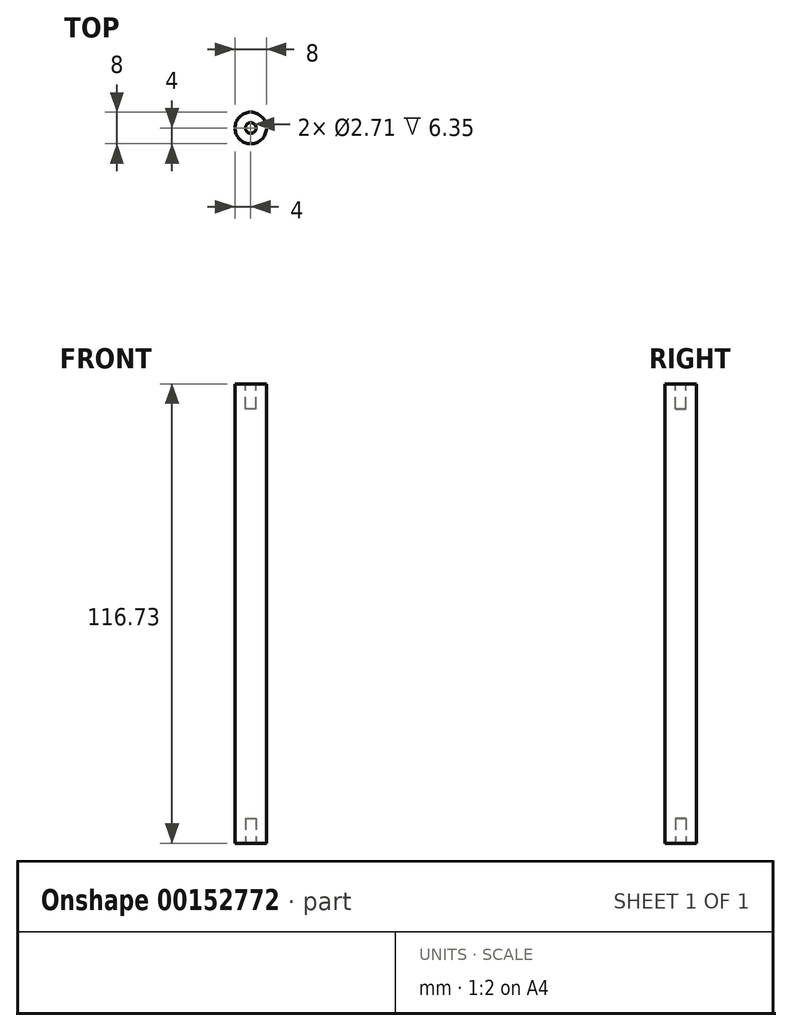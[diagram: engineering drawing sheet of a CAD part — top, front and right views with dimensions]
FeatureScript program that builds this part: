
annotation { "Feature Type Name" : "Feature", "Feature Type Description" : "" }
export const myFeature = defineFeature(function(context is Context, id is Id, definition is map)
    precondition{}
    {
        {
            var Q0;
            Q0=qCreatedBy(makeId("Top.planeOp"),FACE);
            var sketch = newSketch(context, id + "F0", { "sketchPlane" : qUnion([Q0])});
            skCircle(sketch, "E0", {"center": v(0, 0) * mm, "radius": 4 * mm});
            skSolve(sketch);
        }
        {
            var Q0;
            Q0=qSketchRegion(id+"F0",true);
            extrude(context, id + "F1", {"entities" : qUnion([Q0]), "depth" : 116.73 * mm});
        }
        {
            var Q0;
            Q0=makeQuery(id+"F1.opExtrude","CAP_FACE",FACE,{"disambiguationData":[OSD([sQuery(id+"F0.wireOp",EDGE,"E0")])],"isStart":false});
            var sketch = newSketch(context, id + "F2", { "sketchPlane" : qUnion([Q0])});
            skCircle(sketch, "E1", {"center": v(0, 0) * mm, "radius": 1.35 * mm});
            skSolve(sketch);
        }
        {
            var Q0;
            Q0 = qSketchRegion(id + "F2", true);
            extrude(context, id + "F3", {"entities" : qUnion([Q0]), "operationType" : NewBodyOperationType.REMOVE, "oppositeDirection" : true, "depth" : 6.35 * mm});
        }
        {
            var Q0;
            Q0=makeQuery(id+"F1.opExtrude","CAP_FACE",FACE,{"disambiguationData":[OSD([sQuery(id+"F0.wireOp",EDGE,"E0")])],"isStart":true});
            var sketch = newSketch(context, id + "F4", { "sketchPlane" : qUnion([Q0])});
            skCircle(sketch, "E2", {"center": v(0, 0) * mm, "radius": 1.35 * mm});
            skSolve(sketch);
        }
        {
            var Q0;
            Q0 = qSketchRegion(id + "F4", true);
            extrude(context, id + "F5", {"entities" : qUnion([Q0]), "operationType" : NewBodyOperationType.REMOVE, "oppositeDirection" : true, "depth" : 6.35 * mm});
        }
    });
